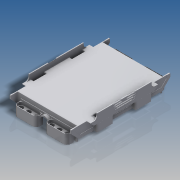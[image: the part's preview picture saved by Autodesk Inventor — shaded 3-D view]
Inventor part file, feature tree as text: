
AUTODESK INVENTOR PART (.ipt)
format: ipt  version: 2016 SP2 (Build 200236200, 236)  size: 1,799,168 bytes
history: native  units: in
note: dims shown in document units (in); Inventor stores cm internally (conversion verified against a paired STEP export)
features: extrude x28, sketch x11, projected_geometry x5, mirror x3, plane x2, fillet x1
ambient origin geometry x8: Origin, YZ Plane, XZ Plane, XY Plane, X Axis, Y Axis, Z Axis, Center Point
bodies: Solid1 (feature_tree)
feature tree (50):
  sketch  "Sketch2"  dims[d1=0.4724in d2=0.1417in]
  extrude  "Extrusion1"  Depth=0.1417in
  extrude  "Extrusion2"  Depth=0.2205in
  extrude  "Extrusion3"  Depth=0.1417in
  extrude  "Extrusion4"  Depth=0.0157in
  extrude  "Extrusion5"  Depth=3.4646in
  extrude  "Extrusion6"  Depth=0.5512in
  sketch  "Sketch3"  dims[d3=4.063in d4=0.2205in]
  extrude  "Extrusion7"  Depth=0.189in
  extrude  "Extrusion8"  Depth=0.2887in
  extrude  "Extrusion9"  Depth=2.7402in TaperAngle=0.0deg
  extrude  "Extrusion11"  Depth=2.4252in TaperAngle=0.0deg
  extrude  "Extrusion12"  Depth=0.0157in TaperAngle=0.0deg
  extrude  "Extrusion13"  Depth=0.126in
  extrude  "Extrusion14"  Depth=0.0157in
  extrude  "Extrusion15"  Depth=0.0157in
  mirror  "Mirror1"
  sketch  "Sketch6"  dims[d9=3.4961in d10=3.4646in]
  extrude  "Extrusion17"  Depth=0.0157in
  extrude  "Extrusion16"  Depth=0.0157in
  extrude  "Extrusion18"  Depth=0.0945in
  extrude  "Extrusion19"  Depth=0.1417in
  plane  "Work Plane1"
  sketch  "Sketch7"  dims[d12=0.5827in d13=0.5512in]
  extrude  "Extrusion21"  Depth=0.0315in
  extrude  "Extrusion22"  Depth=0.0157in
  extrude  "Extrusion23"  Depth=0.0157in TaperAngle=0.0deg
  extrude  "Extrusion24"  Depth=0.1417in TaperAngle=0.0deg
  mirror  "Mirror2"
  mirror  "Mirror3"
  extrude  "Extrusion25"  Depth=0.1417in TaperAngle=0.0deg
  sketch  "Sketch10"  dims[d21=2.8189in d22=0.0in d23=2.7402in d24=0.0in]
  extrude  "Extrusion26"  Depth=0.1417in TaperAngle=0.0deg
  extrude  "Extrusion27"  Depth=0.0157in
  sketch  "Sketch11"  dims[d25=2.5197in d26=0.0in d27=2.4252in d28=0.0in]
  extrude  "Extrusion28"  Depth=0.0157in
  plane  "Work Plane2"
  extrude  "Extrusion29"  Depth=0.0157in
  extrude  "Extrusion30"  Depth=0.0157in
  fillet  "Fillet1"  Radius=0.1102in
  sketch  "Sketch4"  dims[d5=0.1417in d6=0.378in]
  sketch  "Sketch5"  dims[d7=2.4882in d8=0.0157in]
  projected_geometry  "Projected Loop1"
  projected_geometry  "Projected Loop2"
  projected_geometry  "Projected Loop3"
  sketch  "Sketch8"  dims[d16=0.4803in d17=0.189in]
  sketch  "Sketch9"  dims[d19=0.4724in d20=0.2887in]
  projected_geometry  "Projected Loop4"
  sketch  "Sketch12"  dims[d29=2.4252in d30=0.0in d31=2.0787in d32=0.0in d33=0.126in d34=0.0472in d35=0.0472in d36=0.6299in d37=0.9449in d38=0.0945in d39=0.1417in d40=0.0315in d41=0.0472in d42=0.5354in d43=0.0in d44=0.1417in d45=0.0in d46=0.1417in d47=0.0in d50=0.1417in d51=0.0in d52=0.0787in d53=0.189in d54=0.5354in d55=0.6299in d56=0.1102in d57=0.2047in d58=0.0in d59=0.2047in d60=0.0in d61=0.0787in d62=0.0787in d63=0.0472in d64=0.0in d65=0.1225in d66=0.1417in d67=0.1417in d68=0.1225in d69=0.1417in d70=0.0079in d71=0.0in d72=2.1732in d73=0.4094in d74=0.0157in d75=0.0in d76=0.6614in d77=0.3465in d78=0.3622in d79=0.0394in d80=0.0in d81=0.3937in d82=0.063in d83=0.1969in d84=0.1969in d85=0.126in d86=0.0in d87=0.126in d88=0.0in d89=0.063in d90=0.2835in d91=0.6299in d92=0.189in d93=0.2441in d94=45.0deg d97=0.3937in d98=0.0in d99=0.252in d100=0.0in d101=0.0315in d102=0.0in d103=0.1102in d104=0.0in d105=0.063in d106=0.126in d107=0.0in d108=1.126in d109=0.0358in d110=0.298in d111=0.3236in d112=0.298in d113=0.3236in d114=0.8118in d115=0.9618in d116=0.0394in d117=0.0394in d118=0.0394in d119=0.022in d120=0.022in d121=0.022in d122=0.0772in d123=0.0772in d124=0.0772in d125=0.0189in d126=0.126in d127=0.0in d128=0.0079in d129=0.0in d130=0.1937in d131=0.0866in d132=0.9606in d133=0.0079in d134=0.0in d135=0.0079in d136=0.0315in d137=0.3469in d138=0.0in d140=0.0787in d141=0.3386in d142=0.4921in d143=0.1528in d144=0.0787in d145=0.3386in d146=0.0in d147=0.0in d148=0.0039in d149=0.0157in d150=2.5197in]
  projected_geometry  "Projected Loop5"
